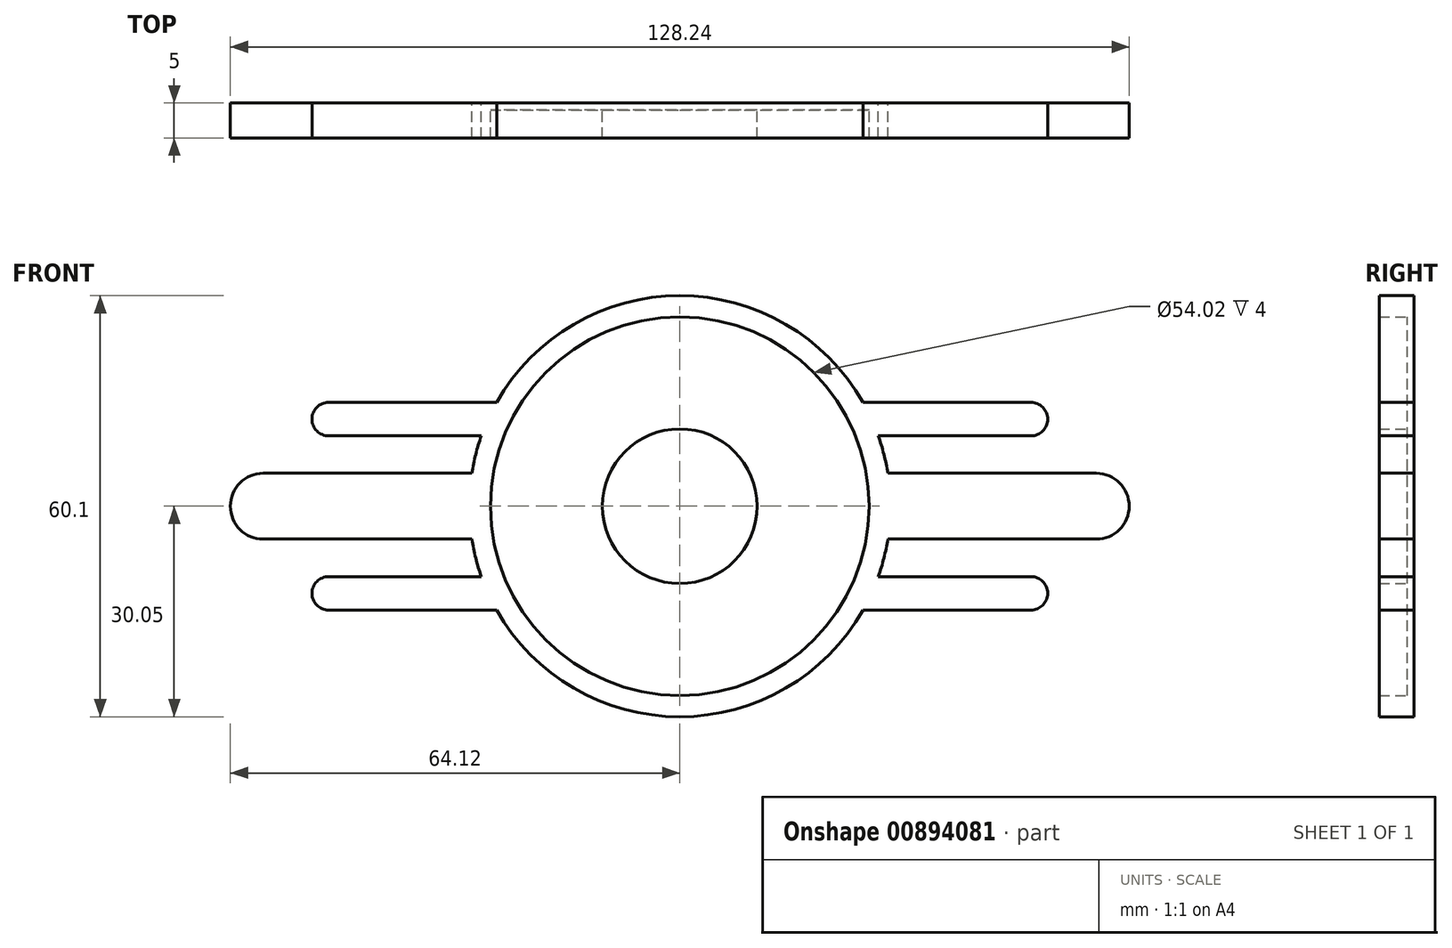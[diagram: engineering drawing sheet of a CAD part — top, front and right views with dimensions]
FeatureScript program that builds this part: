
annotation { "Feature Type Name" : "Feature", "Feature Type Description" : "" }
export const myFeature = defineFeature(function(context is Context, id is Id, definition is map)
    precondition{}
    {
        {
            var Q0;
            Q0=qCreatedBy(makeId("Front.planeOp"),FACE);
            var sketch = newSketch(context, id + "F0", { "sketchPlane" : qUnion([Q0])});
            skCircle(sketch, "E0", {"center": v(0, 0) * mm, "radius": 11.04 * mm});
            skCircle(sketch, "E1", {"center": v(0, 0) * mm, "radius": 27.01 * mm});
            skCircle(sketch, "E2", {"center": v(0, 0) * mm, "radius": 30.05 * mm});
            skLineSegment(sketch, "E3.MirrorCS", {"start": v(29.68, 4.7) * mm, "end": v(59.42, 4.7) * mm});
            skLineSegment(sketch, "E4.MirrorCS", {"start": v(29.68, -4.7) * mm, "end": v(59.42, -4.7) * mm});
            skArc(sketch, "E5.MirrorCS", {"start": v(59.42, 4.7) * mm, "mid": v(64.12, 0) * mm, "end": v(59.42, -4.7) * mm});
            skPoint(sketch, "E6.MirrorCS.start.orphan", {"position": v(-19.12, 23.18) * mm});
            skPoint(sketch, "E7.start.orphan", {"position": v(-37.23, 23.18) * mm});
            skPoint(sketch, "E8.MirrorCS.end.orphan", {"position": v(-37.23, 17.63) * mm});
            skPoint(sketch, "E8.MirrorCS.start.orphan", {"position": v(-24.33, 17.63) * mm});
            skPoint(sketch, "E9.MirrorCS.start.orphan", {"position": v(-29.68, 4.7) * mm});
            skPoint(sketch, "E10.start.orphan", {"position": v(-29.68, -4.7) * mm});
            skPoint(sketch, "E11.end.orphan", {"position": v(-59.42, -4.7) * mm});
            skPoint(sketch, "E11.start.orphan", {"position": v(-59.42, 4.7) * mm});
            skPoint(sketch, "E12.MirrorCS.end.orphan", {"position": v(37.23, 23.18) * mm});
            skPoint(sketch, "E12.MirrorCS.start.orphan", {"position": v(19.12, 23.18) * mm});
            skPoint(sketch, "E13.MirrorCS.end.orphan", {"position": v(37.23, 17.63) * mm});
            skPoint(sketch, "E14.MirrorCS.start.orphan", {"position": v(24.33, 17.63) * mm});
            skPoint(sketch, "E15.MirrorCS.end.orphan", {"position": v(37.23, -17.63) * mm});
            skPoint(sketch, "E15.MirrorCS.start.orphan", {"position": v(24.33, -17.63) * mm});
            skPoint(sketch, "E16.MirrorCS.end.orphan", {"position": v(37.23, -23.18) * mm});
            skPoint(sketch, "E16.MirrorCS.start.orphan", {"position": v(19.12, -23.18) * mm});
            skPoint(sketch, "E17.start.orphan", {"position": v(-24.33, -17.63) * mm});
            skPoint(sketch, "E18.start.orphan", {"position": v(-37.23, -17.63) * mm});
            skPoint(sketch, "E19.end.orphan", {"position": v(-37.23, -23.18) * mm});
            skPoint(sketch, "E19.start.orphan", {"position": v(-19.12, -23.18) * mm});
            skLineSegment(sketch, "E20.MirrorCS", {"start": v(-29.68, 4.7) * mm, "end": v(-59.42, 4.7) * mm});
            skLineSegment(sketch, "E21.MirrorCS", {"start": v(-29.68, -4.7) * mm, "end": v(-59.42, -4.7) * mm});
            skArc(sketch, "E22.MirrorCS", {"start": v(-59.42, 4.7) * mm, "mid": v(-64.12, 0) * mm, "end": v(-59.42, -4.7) * mm});
            skLineSegment(sketch, "E23", {"start": v(-28.32, 10.04) * mm, "end": v(-50.1, 10.04) * mm});
            skLineSegment(sketch, "E24", {"start": v(-26.14, 14.82) * mm, "end": v(-50.1, 14.82) * mm});
            skLineSegment(sketch, "E25.MirrorCS", {"start": v(-28.32, -10.04) * mm, "end": v(-50.1, -10.04) * mm});
            skLineSegment(sketch, "E26.MirrorCS", {"start": v(-26.14, -14.82) * mm, "end": v(-50.1, -14.82) * mm});
            skLineSegment(sketch, "E27.MirrorCS", {"start": v(26.14, 14.82) * mm, "end": v(50.1, 14.82) * mm});
            skLineSegment(sketch, "E28.MirrorCS", {"start": v(28.32, 10.04) * mm, "end": v(50.1, 10.04) * mm});
            skLineSegment(sketch, "E29.MirrorCS", {"start": v(28.32, -10.04) * mm, "end": v(50.1, -10.04) * mm});
            skLineSegment(sketch, "E30.MirrorCS", {"start": v(26.14, -14.82) * mm, "end": v(50.1, -14.82) * mm});
            skArc(sketch, "E31", {"start": v(50.1, 10.04) * mm, "mid": v(52.5, 12.43) * mm, "end": v(50.1, 14.82) * mm});
            skArc(sketch, "E32", {"start": v(50.1, -14.82) * mm, "mid": v(52.5, -12.43) * mm, "end": v(50.1, -10.04) * mm});
            skArc(sketch, "E33.MirrorCS", {"start": v(-50.1, 10.04) * mm, "mid": v(-52.5, 12.43) * mm, "end": v(-50.1, 14.82) * mm});
            skArc(sketch, "E34.MirrorCS", {"start": v(-50.1, -14.82) * mm, "mid": v(-52.5, -12.43) * mm, "end": v(-50.1, -10.04) * mm});
            skSolve(sketch);
        }
        {
            var Q0;
            Q0=makeQuery(id+"F0.imprint","IMPRINT",FACE,{"disambiguationData":[TD([[makeQuery(id+"F0.imprint","IMPRINT",EDGE,{"derivedFrom":sQuery(id+"F0.wireOp",EDGE,"E0")}),-1.0]])]});
            extrude(context, id + "F1", {"entities" : qUnion([Q0]), "depth" : 1 * mm, "offsetDistance" : 25.4 * mm});
        }
        {
            var Q0;
            Q0=makeQuery(id+"F0.imprint","IMPRINT",FACE,{"disambiguationData":[TD([[makeQuery(id+"F0.imprint","IMPRINT",EDGE,{"derivedFrom":sQuery(id+"F0.wireOp",EDGE,"E1")}),-1.0]])]});
            var Q1;
            Q1=makeQuery(id+"F0.imprint","IMPRINT",FACE,{"disambiguationData":[TD([[makeQuery(id+"F0.imprint","IMPRINT",EDGE,{"derivedFrom":sQuery(id+"F0.wireOp",EDGE,"E0")}),1.0]])]});
            var Q2;
            {var subQ0=sQuery(id+"F0.wireOp",EDGE,"E27.MirrorCS");Q2=makeQuery(id+"F0.imprint","IMPRINT",FACE,{"disambiguationData":[TD([[makeQuery(id+"F0.imprint","IMPRINT",EDGE,{"derivedFrom":subQ0}),-1.0]])]});}
            var Q3;
            {var subQ0=sQuery(id+"F0.wireOp",EDGE,"E3.MirrorCS");Q3=makeQuery(id+"F0.imprint","IMPRINT",FACE,{"disambiguationData":[TD([[makeQuery(id+"F0.imprint","IMPRINT",EDGE,{"derivedFrom":subQ0}),-1.0]])]});}
            var Q4;
            {var subQ0=sQuery(id+"F0.wireOp",EDGE,"E29.MirrorCS");Q4=makeQuery(id+"F0.imprint","IMPRINT",FACE,{"disambiguationData":[TD([[makeQuery(id+"F0.imprint","IMPRINT",EDGE,{"derivedFrom":subQ0}),-1.0]])]});}
            var Q5;
            {var subQ0=sQuery(id+"F0.wireOp",EDGE,"E25.MirrorCS");Q5=makeQuery(id+"F0.imprint","IMPRINT",FACE,{"disambiguationData":[TD([[makeQuery(id+"F0.imprint","IMPRINT",EDGE,{"derivedFrom":subQ0}),1.0]])]});}
            var Q6;
            {var subQ0=sQuery(id+"F0.wireOp",EDGE,"E20.MirrorCS");Q6=makeQuery(id+"F0.imprint","IMPRINT",FACE,{"disambiguationData":[TD([[makeQuery(id+"F0.imprint","IMPRINT",EDGE,{"derivedFrom":subQ0}),1.0]])]});}
            var Q7;
            {var subQ0=sQuery(id+"F0.wireOp",EDGE,"E23");Q7=makeQuery(id+"F0.imprint","IMPRINT",FACE,{"disambiguationData":[TD([[makeQuery(id+"F0.imprint","IMPRINT",EDGE,{"derivedFrom":subQ0}),-1.0]])]});}
            extrude(context, id + "F2", {"entities" : qUnion([Q0, Q1, Q2, Q3, Q4, Q5, Q6, Q7]), "operationType" : NewBodyOperationType.ADD, "depth" : 5 * mm, "offsetDistance" : 25.4 * mm});
        }
    });
